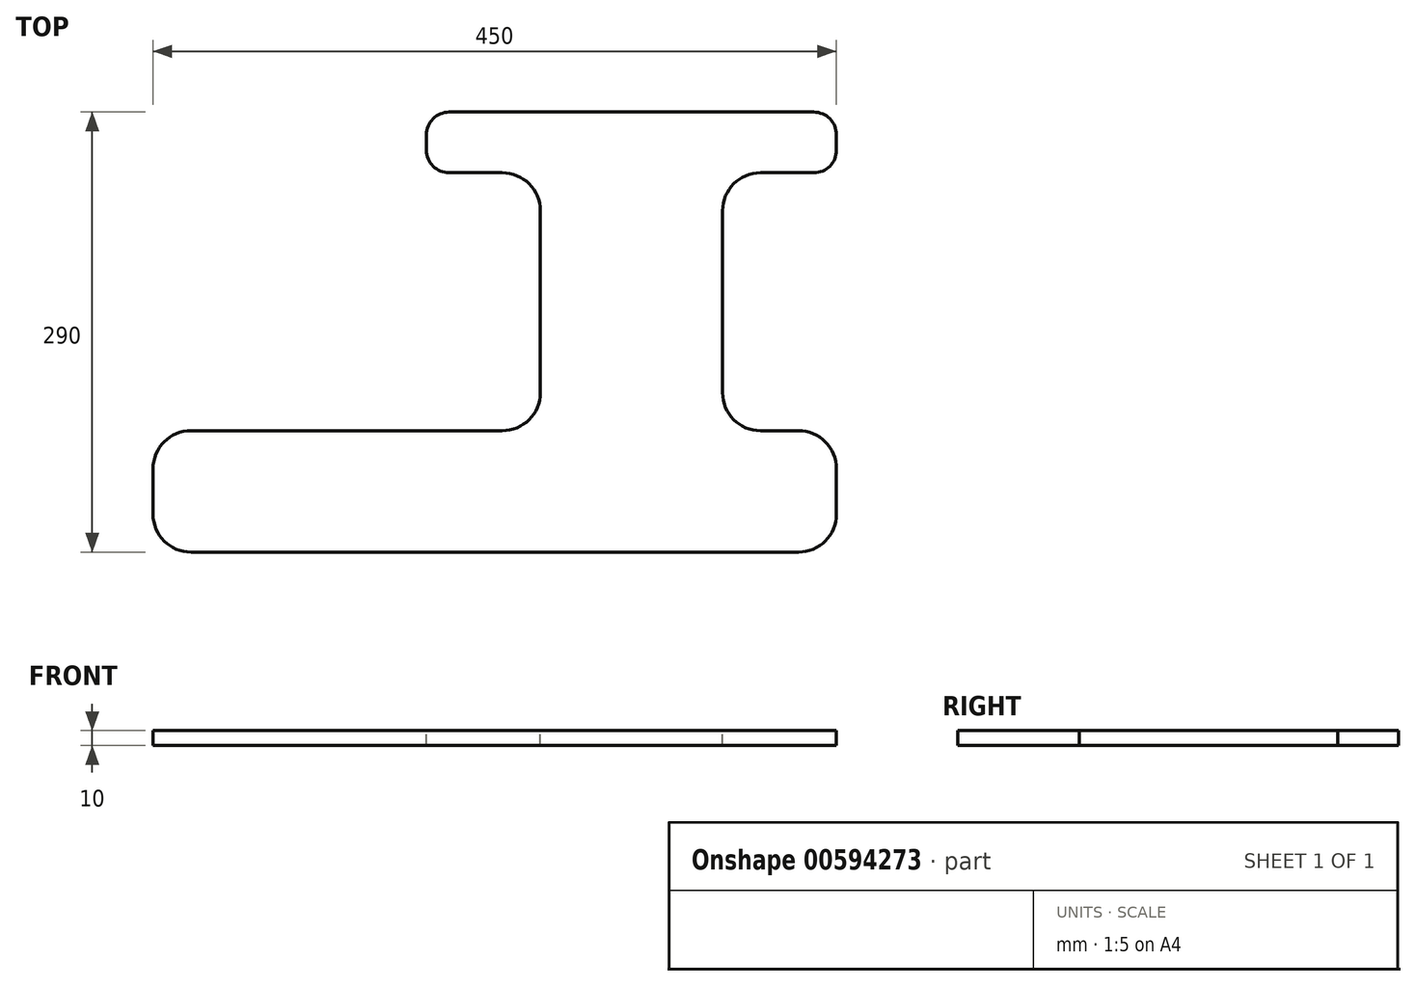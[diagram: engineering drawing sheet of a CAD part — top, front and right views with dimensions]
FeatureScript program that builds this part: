
annotation { "Feature Type Name" : "Feature", "Feature Type Description" : "" }
export const myFeature = defineFeature(function(context is Context, id is Id, definition is map)
    precondition{}
    {
        {
            var Q0;
            Q0=qCreatedBy(makeId("Top.planeOp"),FACE);
            var sketch = newSketch(context, id + "F0", { "sketchPlane" : qUnion([Q0])});
            skLineSegment(sketch, "E0.bottom", {"start": v(-120, 40) * mm, "end": v(-275, 40) * mm});
            skLineSegment(sketch, "E0.top", {"start": v(125, -40) * mm, "end": v(-275, -40) * mm});
            skPoint(sketch, "E0.middle", {"position": v(0, 0) * mm});
            skLineSegment(sketch, "E1", {"start": v(150, -15) * mm, "end": v(150, 15) * mm});
            skLineSegment(sketch, "E2.top", {"start": v(135, 250) * mm, "end": v(-105, 250) * mm});
            skLineSegment(sketch, "E2.left", {"start": v(150, 40) * mm, "end": v(150, 210) * mm, "construction": true});
            skLineSegment(sketch, "E2.right", {"start": v(-120, 40) * mm, "end": v(-120, 210) * mm, "construction": true});
            skLineSegment(sketch, "E3", {"start": v(0, 0) * mm, "end": v(-428.9, 0) * mm, "construction": true});
            skLineSegment(sketch, "E4", {"start": v(-300, -15) * mm, "end": v(-300, 0) * mm});
            skLineSegment(sketch, "E5", {"start": v(-300, 0) * mm, "end": v(-300, 15) * mm});
            skLineSegment(sketch, "E6.0", {"start": v(-45, 65) * mm, "end": v(-45, 185) * mm});
            skLineSegment(sketch, "E7.0", {"start": v(75, 65) * mm, "end": v(75, 185) * mm});
            skLineSegment(sketch, "E8.0", {"start": v(135, 210) * mm, "end": v(100, 210) * mm});
            skLineSegment(sketch, "E9", {"start": v(-120, 40) * mm, "end": v(-70, 40) * mm});
            skLineSegment(sketch, "E10", {"start": v(100, 40) * mm, "end": v(125, 40) * mm});
            skLineSegment(sketch, "E11", {"start": v(-120, 225) * mm, "end": v(-120, 235) * mm});
            skLineSegment(sketch, "E12", {"start": v(150, 225) * mm, "end": v(150, 235) * mm});
            skLineSegment(sketch, "E13.trimOffspring", {"start": v(-70, 210) * mm, "end": v(-105, 210) * mm});
            skPoint(sketch, "E14.visualSharp", {"position": v(-300, -40) * mm});
            skArc(sketch, "E14.filletArc", {"start": v(-300, -15) * mm, "mid": v(-292.68, -32.68) * mm, "end": v(-275, -40) * mm});
            skPoint(sketch, "E15.visualSharp", {"position": v(-300, 40) * mm});
            skArc(sketch, "E15.filletArc", {"start": v(-275, 40) * mm, "mid": v(-292.68, 32.68) * mm, "end": v(-300, 15) * mm});
            skPoint(sketch, "E16.visualSharp", {"position": v(-45, 40) * mm});
            skArc(sketch, "E16.filletArc", {"start": v(-70, 40) * mm, "mid": v(-52.32, 47.32) * mm, "end": v(-45, 65) * mm});
            skPoint(sketch, "E17.visualSharp", {"position": v(-45, 210) * mm});
            skArc(sketch, "E17.filletArc", {"start": v(-45, 185) * mm, "mid": v(-52.32, 202.68) * mm, "end": v(-70, 210) * mm});
            skPoint(sketch, "E18.visualSharp", {"position": v(150, -40) * mm});
            skArc(sketch, "E18.filletArc", {"start": v(125, -40) * mm, "mid": v(142.68, -32.68) * mm, "end": v(150, -15) * mm});
            skPoint(sketch, "E19.visualSharp", {"position": v(150, 40) * mm});
            skArc(sketch, "E19.filletArc", {"start": v(150, 15) * mm, "mid": v(142.68, 32.68) * mm, "end": v(125, 40) * mm});
            skPoint(sketch, "E20.visualSharp", {"position": v(75, 210) * mm});
            skArc(sketch, "E20.filletArc", {"start": v(100, 210) * mm, "mid": v(82.32, 202.68) * mm, "end": v(75, 185) * mm});
            skPoint(sketch, "E21.visualSharp", {"position": v(75, 40) * mm});
            skArc(sketch, "E21.filletArc", {"start": v(75, 65) * mm, "mid": v(82.32, 47.32) * mm, "end": v(100, 40) * mm});
            skPoint(sketch, "E22.visualSharp", {"position": v(-120, 210) * mm});
            skArc(sketch, "E22.filletArc", {"start": v(-120, 225) * mm, "mid": v(-115.6, 214.4) * mm, "end": v(-105, 210) * mm});
            skPoint(sketch, "E23.visualSharp", {"position": v(-120, 250) * mm});
            skArc(sketch, "E23.filletArc", {"start": v(-105, 250) * mm, "mid": v(-115.6, 245.6) * mm, "end": v(-120, 235) * mm});
            skPoint(sketch, "E24.visualSharp", {"position": v(150, 250) * mm});
            skArc(sketch, "E24.filletArc", {"start": v(150, 235) * mm, "mid": v(145.6, 245.6) * mm, "end": v(135, 250) * mm});
            skPoint(sketch, "E25.visualSharp", {"position": v(150, 210) * mm});
            skArc(sketch, "E25.filletArc", {"start": v(135, 210) * mm, "mid": v(145.6, 214.4) * mm, "end": v(150, 225) * mm});
            skSolve(sketch);
        }
        {
            var Q0;
            Q0 = qSketchRegion(id + "F0", true);
            extrude(context, id + "F1", {"entities" : qUnion([Q0]), "oppositeDirection" : true, "depth" : 10 * mm, "offsetDistance" : 25 * mm});
        }
    });
